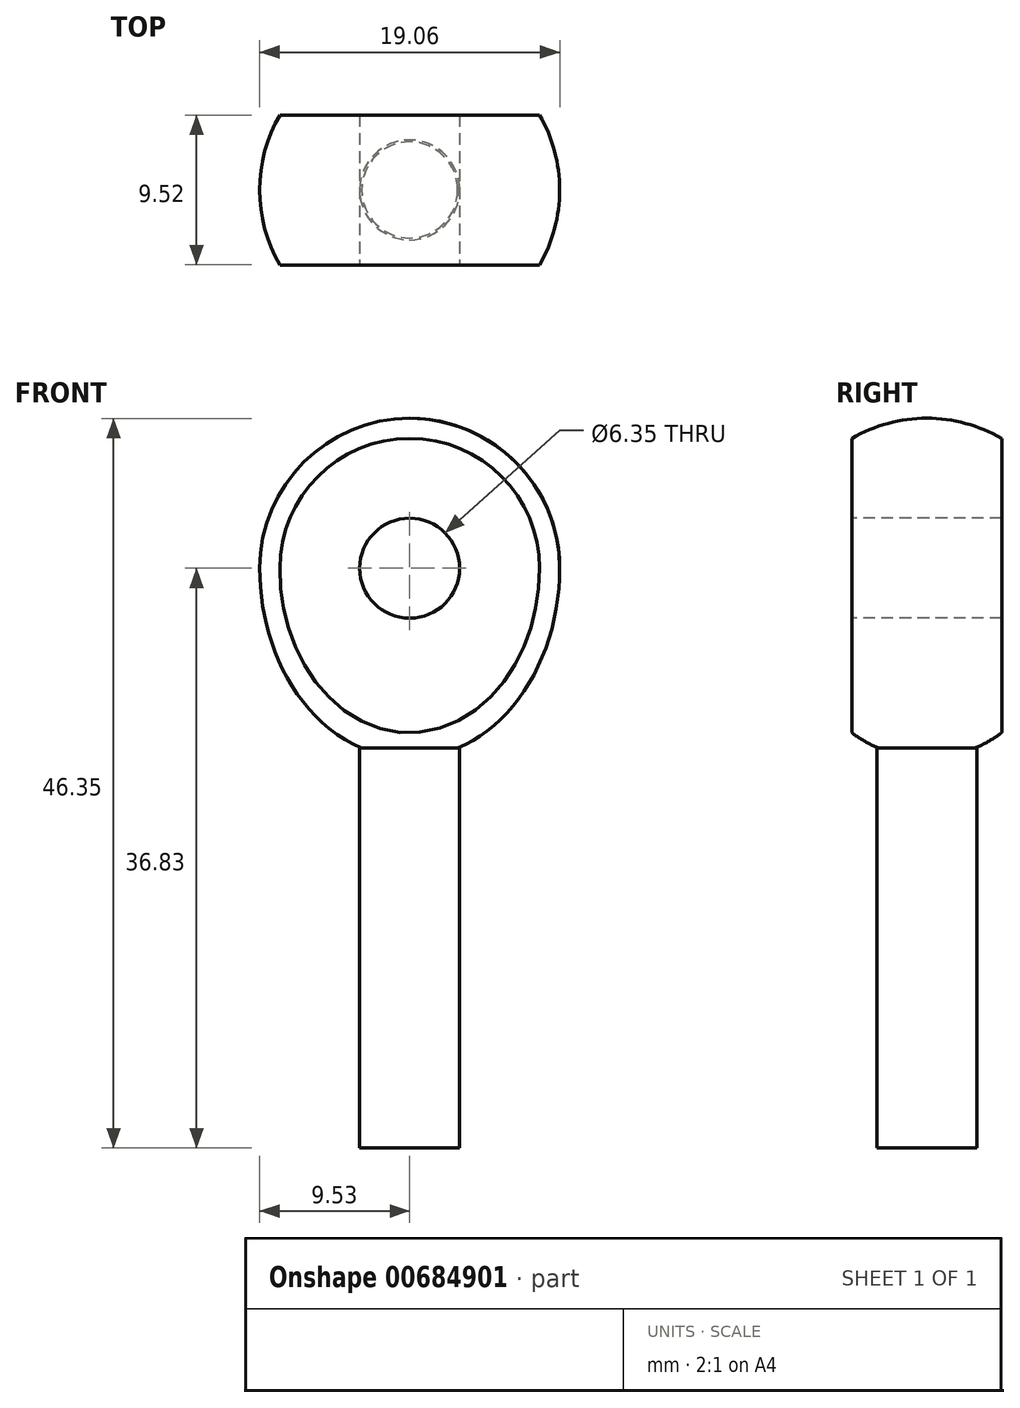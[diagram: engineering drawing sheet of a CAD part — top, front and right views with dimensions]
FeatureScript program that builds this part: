
annotation { "Feature Type Name" : "Feature", "Feature Type Description" : "" }
export const myFeature = defineFeature(function(context is Context, id is Id, definition is map)
    precondition{}
    {
        {
            var Q0;
            Q0=qCreatedBy(makeId("Front.planeOp"),FACE);
            var sketch = newSketch(context, id + "F0", { "sketchPlane" : qUnion([Q0])});
            skArc(sketch, "E0", {"start": v(9.52, 0) * mm, "mid": v(6.74, 6.74) * mm, "end": v(0, 9.52) * mm});
            skEllipticalArc(sketch, "E1", {});
            skLineSegment(sketch, "E2", {"start": v(0, 31.73) * mm, "end": v(0, -27.67) * mm, "construction": true});
            skLineSegment(sketch, "E3", {"start": v(0, 9.52) * mm, "end": v(0, -12.06) * mm});
            const initialGuessF0  = {"E1": [0, 0, 0, 1, 0.012065, 0.009525, 3.141592653589793, 4.71238898038469]};
            skSetInitialGuess(sketch, initialGuessF0);
            skSolve(sketch);
        }
        {
            var Q0;
            Q0 = qSketchRegion(id + "F0", true);
            var Q1;
            Q1=sQuery(id+"F0.wireOp",EDGE,"E2");
            revolve(context, id + "F1", {"surfaceOperationType" : NewSurfaceOperationType.NEW, "entities" : qUnion([Q0]), "axis" : qUnion([Q1]), "revolveType" : RevolveType.FULL});
        }
        {
            var Q0;
            Q0=qCreatedBy(makeId("Top.planeOp"),FACE);
            var sketch = newSketch(context, id + "F2", { "sketchPlane" : qUnion([Q0])});
            skLineSegment(sketch, "E4", {"start": v(-32.12, 0) * mm, "end": v(40.24, 0) * mm, "construction": true});
            skLineSegment(sketch, "E5.bottom", {"start": v(-9.52, 11.11) * mm, "end": v(9.52, 11.11) * mm});
            skLineSegment(sketch, "E5.top", {"start": v(-9.52, 4.76) * mm, "end": v(9.52, 4.76) * mm});
            skLineSegment(sketch, "E5.left", {"start": v(-9.52, 11.11) * mm, "end": v(-9.52, 4.76) * mm});
            skLineSegment(sketch, "E5.right", {"start": v(9.52, 11.11) * mm, "end": v(9.52, 4.76) * mm});
            skLineSegment(sketch, "E6.MirrorCS", {"start": v(9.52, -11.11) * mm, "end": v(9.52, -4.76) * mm});
            skLineSegment(sketch, "E7.MirrorCS", {"start": v(-9.52, -11.11) * mm, "end": v(-9.52, -4.76) * mm});
            skLineSegment(sketch, "E8.MirrorCS", {"start": v(-9.52, -4.76) * mm, "end": v(9.52, -4.76) * mm});
            skLineSegment(sketch, "E9.MirrorCS", {"start": v(-9.52, -11.11) * mm, "end": v(9.52, -11.11) * mm});
            skSolve(sketch);
        }
        {
            var Q0;
            Q0 = qSketchRegion(id + "F2", true);
            extrude(context, id + "F3", {"entities" : qUnion([Q0]), "operationType" : NewBodyOperationType.REMOVE, "depth" : 25.4 * mm, "offsetDistance" : 25.4 * mm, "symmetric" : true});
        }
        {
            var Q0;
            Q0=qCreatedBy(makeId("Front.planeOp"),FACE);
            var sketch = newSketch(context, id + "F4", { "sketchPlane" : qUnion([Q0])});
            skCircle(sketch, "E10", {"center": v(0, 0) * mm, "radius": 3.18 * mm});
            skSolve(sketch);
        }
        {
            var Q0;
            Q0 = qSketchRegion(id + "F4", true);
            extrude(context, id + "F5", {"entities" : qUnion([Q0]), "operationType" : NewBodyOperationType.REMOVE, "oppositeDirection" : true, "depth" : 25.4 * mm, "offsetDistance" : 25.4 * mm, "symmetric" : true});
        }
        {
            var Q0;
            Q0=qCreatedBy(makeId("Top.planeOp"),FACE);
            cPlane(context, id + "F6", {"entities" : qUnion([Q0]), "cplaneType" : CPlaneType.OFFSET, "offset" : 11.43 * mm, "oppositeDirection" : true, "width" : 152.4 * mm, "height" : 152.4 * mm});
        }
        {
            var Q0;
            Q0=qCreatedBy(id+"F6.planeOp",FACE);
            var sketch = newSketch(context, id + "F7", { "sketchPlane" : qUnion([Q0])});
            skCircle(sketch, "E11", {"center": v(0, 0) * mm, "radius": 3.18 * mm});
            skSolve(sketch);
        }
        {
            var Q0;
            Q0 = qSketchRegion(id + "F7", true);
            extrude(context, id + "F8", {"entities" : qUnion([Q0]), "operationType" : NewBodyOperationType.ADD, "oppositeDirection" : true, "depth" : 25.4 * mm, "offsetDistance" : 25.4 * mm});
        }
    });
